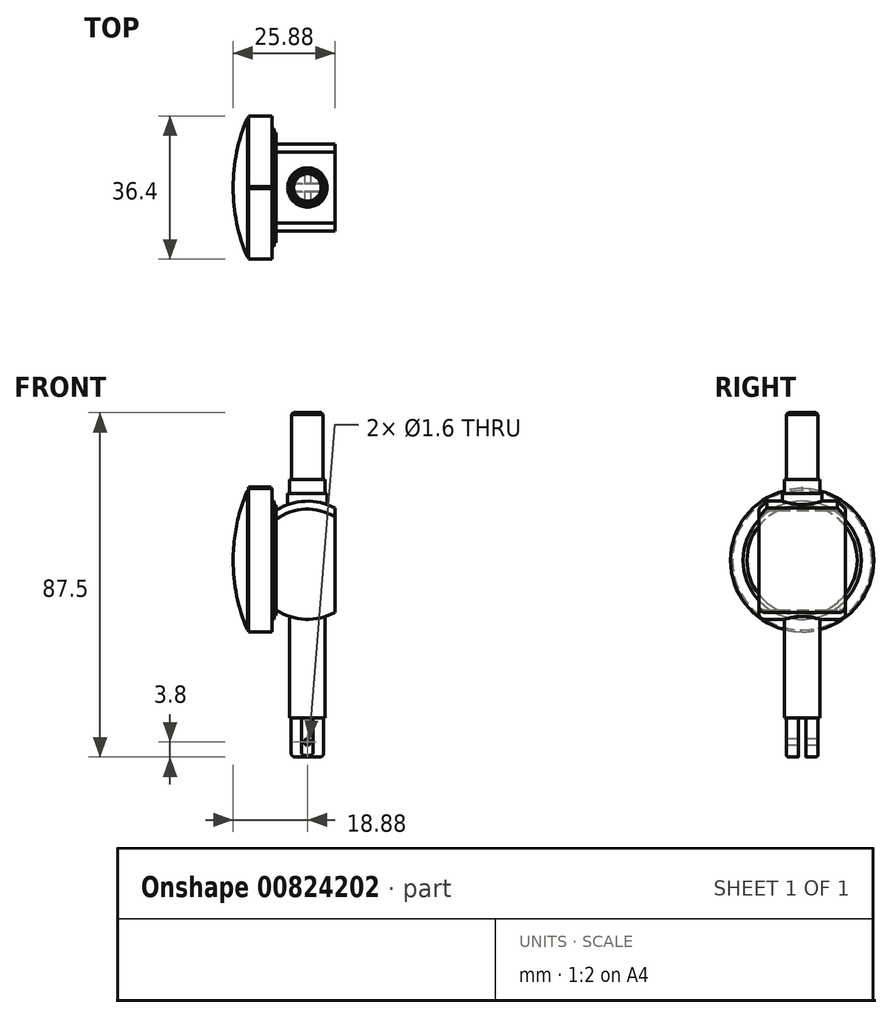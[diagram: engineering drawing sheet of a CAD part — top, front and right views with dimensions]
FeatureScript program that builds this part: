
annotation { "Feature Type Name" : "Feature", "Feature Type Description" : "" }
export const myFeature = defineFeature(function(context is Context, id is Id, definition is map)
    precondition{}
    {
        {
            var Q0;
            Q0=qCreatedBy(makeId("Front.planeOp"),FACE);
            var sketch = newSketch(context, id + "F0", { "sketchPlane" : qUnion([Q0])});
            skArc(sketch, "E0", {"start": v(7, 13.27) * mm, "mid": v(-0.58, 14.99) * mm, "end": v(-8, 12.69) * mm});
            skLineSegment(sketch, "E1", {"start": v(7, 13.27) * mm, "end": v(7, -13.27) * mm});
            skLineSegment(sketch, "E2", {"start": v(-8, 12.69) * mm, "end": v(-8, -12.69) * mm});
            skArc(sketch, "E3.trimOffspring", {"start": v(-8, -12.69) * mm, "mid": v(-0.58, -14.99) * mm, "end": v(7, -13.27) * mm});
            skSolve(sketch);
        }
        {
            var Q0;
            Q0=makeQuery(id+"F0.imprint","IMPRINT",FACE,{"disambiguationData":[TD([[makeQuery(id+"F0.imprint","IMPRINT",EDGE,{"derivedFrom":sQuery(id+"F0.wireOp",EDGE,"E0")}),1.0]])]});
            extrude(context, id + "F1", {"entities" : qUnion([Q0]), "endBound" : BoundingType.SYMMETRIC, "depth" : 22 * mm, "offsetDistance" : 25 * mm});
        }
        {
            var Q0;
            Q0=makeQuery(id+"F1.opExtrude","CAP_EDGE",EDGE,{"disambiguationData":[OSD([sQuery(id+"F0.wireOp",EDGE,"E0")])],"isStart":false});
            var Q1;
            Q1=makeQuery(id+"F1.opExtrude","CAP_EDGE",EDGE,{"disambiguationData":[OSD([sQuery(id+"F0.wireOp",EDGE,"E0")])],"isStart":true});
            chamfer(context, id + "F2", {"entities" : qUnion([Q0, Q1]), "width" : 2 * mm, "tangentPropagation" : true});
        }
        {
            var Q0;
            Q0=makeQuery(id+"F1.opExtrude","CAP_EDGE",EDGE,{"disambiguationData":[OSD([sQuery(id+"F0.wireOp",EDGE,"E3.trimOffspring")])],"isStart":false});
            var Q1;
            Q1=makeQuery(id+"F1.opExtrude","CAP_EDGE",EDGE,{"disambiguationData":[OSD([sQuery(id+"F0.wireOp",EDGE,"E3.trimOffspring")])],"isStart":true});
            fillet(context, id + "F3", {"entities" : qUnion([Q0, Q1]), "radius" : 1.5 * mm, "tangentPropagation" : true, "allowEdgeOverflow" : false});
        }
        {
            var Q0;
            Q0=qCreatedBy(makeId("Top.planeOp"),FACE);
            var sketch = newSketch(context, id + "F4", { "sketchPlane" : qUnion([Q0])});
            skCircle(sketch, "E4", {"center": v(0, 0) * mm, "radius": 5 * mm});
            skSolve(sketch);
        }
        {
            var Q0;
            Q0 = qSketchRegion(id + "F4", true);
            extrude(context, id + "F5", {"entities" : qUnion([Q0]), "operationType" : NewBodyOperationType.ADD, "depth" : 17 * mm, "offsetDistance" : 25 * mm});
        }
        {
            var Q0;
            Q0=makeQuery(id+"F5.opExtrude","CAP_FACE",FACE,{"disambiguationData":[OSD([sQuery(id+"F4.wireOp",EDGE,"E4")])],"isStart":false});
            var sketch = newSketch(context, id + "F6", { "sketchPlane" : qUnion([Q0])});
            skCircle(sketch, "E5", {"center": v(0, 0) * mm, "radius": 4.5 * mm});
            skSolve(sketch);
        }
        {
            var Q0;
            Q0=makeQuery(id+"F6.imprint","IMPRINT",FACE,{"disambiguationData":[TD([[makeQuery(id+"F6.imprint","IMPRINT",EDGE,{"derivedFrom":sQuery(id+"F6.wireOp",EDGE,"E5")}),1.0]])]});
            extrude(context, id + "F7", {"entities" : qUnion([Q0]), "operationType" : NewBodyOperationType.ADD, "depth" : 3.5 * mm, "offsetDistance" : 25 * mm});
        }
        {
            var Q0;
            Q0=makeQuery(id+"F7.opExtrude","CAP_FACE",FACE,{"disambiguationData":[OSD([sQuery(id+"F6.wireOp",EDGE,"E5")])],"isStart":false});
            var sketch = newSketch(context, id + "F8", { "sketchPlane" : qUnion([Q0])});
            skCircle(sketch, "E6", {"center": v(0, 0) * mm, "radius": 4 * mm});
            skSolve(sketch);
        }
        {
            var Q0;
            Q0=makeQuery(id+"F8.imprint","IMPRINT",FACE,{"disambiguationData":[TD([[makeQuery(id+"F8.imprint","IMPRINT",EDGE,{"derivedFrom":sQuery(id+"F8.wireOp",EDGE,"E6")}),1.0]])]});
            var Q1;
            Q1 = qSketchRegion(id + "F11", true);
            extrude(context, id + "F9", {"entities" : qUnion([Q0, Q1]), "operationType" : NewBodyOperationType.ADD, "depth" : 17 * mm, "offsetDistance" : 25 * mm});
        }
        {
            var Q0;
            Q0=makeQuery(id+"F9.opExtrude","CAP_EDGE",EDGE,{"disambiguationData":[OSD([sQuery(id+"F8.wireOp",EDGE,"E6")])],"isStart":false});
            chamfer(context, id + "F10", {"entities" : qUnion([Q0]), "width" : 0.5 * mm, "tangentPropagation" : true});
        }
        {
            var Q0;
            Q0=qCreatedBy(makeId("Top.planeOp"),FACE);
            var sketch = newSketch(context, id + "F11", { "sketchPlane" : qUnion([Q0])});
            skCircle(sketch, "E7", {"center": v(0, 0) * mm, "radius": 4.5 * mm});
            skSolve(sketch);
        }
        {
            var Q0;
            Q0 = qSketchRegion(id + "F11", true);
            extrude(context, id + "F12", {"entities" : qUnion([Q0]), "operationType" : NewBodyOperationType.ADD, "oppositeDirection" : true, "depth" : 40 * mm, "offsetDistance" : 25 * mm});
        }
        {
            var Q0;
            Q0=makeQuery(id+"F12.opExtrude","CAP_FACE",FACE,{"disambiguationData":[OSD([sQuery(id+"F11.wireOp",EDGE,"E7")])],"isStart":false});
            var sketch = newSketch(context, id + "F13", { "sketchPlane" : qUnion([Q0])});
            skCircle(sketch, "E8", {"center": v(0, 0) * mm, "radius": 4.25 * mm});
            skSolve(sketch);
        }
        {
            var Q0;
            Q0=makeQuery(id+"F13.imprint","IMPRINT",FACE,{"disambiguationData":[TD([[makeQuery(id+"F13.imprint","IMPRINT",EDGE,{"derivedFrom":sQuery(id+"F13.wireOp",EDGE,"E8")}),1.0]])]});
            extrude(context, id + "F14", {"entities" : qUnion([Q0]), "operationType" : NewBodyOperationType.ADD, "depth" : 10 * mm, "offsetDistance" : 25 * mm});
        }
        {
            var Q0;
            Q0=makeQuery(id+"F14.opExtrude","CAP_EDGE",EDGE,{"disambiguationData":[OSD([sQuery(id+"F13.wireOp",EDGE,"E8")])],"isStart":false});
            fillet(context, id + "F15", {"entities" : qUnion([Q0]), "radius" : 1 * mm, "tangentPropagation" : true, "allowEdgeOverflow" : false});
        }
        {
            var Q0;
            Q0=qCreatedBy(makeId("Front.planeOp"),FACE);
            var sketch = newSketch(context, id + "F16", { "sketchPlane" : qUnion([Q0])});
            skLineSegment(sketch, "E9.0", {"start": v(-8, 10.25) * mm, "end": v(-8, -10.87) * mm});
            skLineSegment(sketch, "E10", {"start": v(-8, 0) * mm, "end": v(-8, 14) * mm});
            skLineSegment(sketch, "E11", {"start": v(-8, 14) * mm, "end": v(-8.5, 14) * mm});
            skLineSegment(sketch, "E12", {"start": v(-8.5, 14) * mm, "end": v(-8.5, 15) * mm});
            skLineSegment(sketch, "E13", {"start": v(-8.5, 15) * mm, "end": v(-9, 15) * mm});
            skLineSegment(sketch, "E14", {"start": v(-9, 15) * mm, "end": v(-9, 18.2) * mm});
            skLineSegment(sketch, "E15", {"start": v(-15, 18.2) * mm, "end": v(-9, 18.2) * mm});
            skLineSegment(sketch, "E16", {"start": v(-15, 17.7) * mm, "end": v(-15.25, 17.7) * mm});
            skLineSegment(sketch, "E17", {"start": v(-15, 18.2) * mm, "end": v(-15, 17.7) * mm});
            skLineSegment(sketch, "E18", {"start": v(-8, 0) * mm, "end": v(-18.88, 0) * mm});
            skArc(sketch, "E19", {"start": v(-15.25, 17.7) * mm, "mid": v(-17.96, 9.03) * mm, "end": v(-18.88, 0) * mm});
            skSolve(sketch);
        }
        {
            var Q0;
            {var subQ0=sQuery(id+"F16.wireOp",EDGE,"E11");Q0=makeQuery(id+"F16.imprint","IMPRINT",FACE,{"disambiguationData":[TD([[makeQuery(id+"F16.imprint","IMPRINT",EDGE,{"derivedFrom":subQ0}),1.0]])]});}
            var Q1;
            Q1=sQuery(id+"F16.wireOp",EDGE,"E18");
            revolve(context, id + "F17", {"operationType" : NewBodyOperationType.ADD, "surfaceOperationType" : NewSurfaceOperationType.NEW, "entities" : qUnion([Q0]), "axis" : qUnion([Q1]), "revolveType" : RevolveType.FULL});
        }
        {
            var Q0;
            Q0=qCreatedBy(makeId("Right.planeOp"),FACE);
            var sketch = newSketch(context, id + "F18", { "sketchPlane" : qUnion([Q0])});
            skLineSegment(sketch, "E20.0", {"start": v(-4.5, -40) * mm, "end": v(4.5, -40) * mm, "construction": true});
            skLineSegment(sketch, "E21.bottom", {"start": v(-1, -40) * mm, "end": v(1, -40) * mm});
            skLineSegment(sketch, "E21.top", {"start": v(-1, -51) * mm, "end": v(1, -51) * mm});
            skLineSegment(sketch, "E21.left", {"start": v(-1, -40) * mm, "end": v(-1, -51) * mm});
            skLineSegment(sketch, "E21.right", {"start": v(1, -40) * mm, "end": v(1, -51) * mm});
            skLineSegment(sketch, "E22.bottom", {"start": v(-4, -40) * mm, "end": v(-6, -40) * mm});
            skLineSegment(sketch, "E22.top", {"start": v(-4, -51) * mm, "end": v(-6, -51) * mm});
            skLineSegment(sketch, "E22.left", {"start": v(-4, -40) * mm, "end": v(-4, -51) * mm});
            skLineSegment(sketch, "E22.right", {"start": v(-6, -40) * mm, "end": v(-6, -51) * mm});
            skLineSegment(sketch, "E23.bottom", {"start": v(4, -40) * mm, "end": v(6, -40) * mm});
            skLineSegment(sketch, "E23.top", {"start": v(4, -51) * mm, "end": v(6, -51) * mm});
            skLineSegment(sketch, "E23.left", {"start": v(4, -40) * mm, "end": v(4, -51) * mm});
            skLineSegment(sketch, "E23.right", {"start": v(6, -40) * mm, "end": v(6, -51) * mm});
            skLineSegment(sketch, "E24.0", {"start": v(3.25, -50) * mm, "end": v(-3.25, -50) * mm, "construction": true});
            skLineSegment(sketch, "E25", {"start": v(-4.5, -40) * mm, "end": v(-1, -40) * mm});
            skLineSegment(sketch, "E26", {"start": v(1, -40) * mm, "end": v(4.5, -40) * mm});
            skLineSegment(sketch, "E27", {"start": v(-4, -42.75) * mm, "end": v(-1, -42.75) * mm, "construction": true});
            skLineSegment(sketch, "E28", {"start": v(1, -45.5) * mm, "end": v(4, -45.5) * mm, "construction": true});
            skSolve(sketch);
        }
        {
            var Q0;
            Q0 = qSketchRegion(id + "F18", true);
            extrude(context, id + "F19", {"entities" : qUnion([Q0]), "operationType" : NewBodyOperationType.REMOVE, "endBound" : BoundingType.SYMMETRIC, "oppositeDirection" : true, "depth" : 25 * mm, "offsetDistance" : 25 * mm});
        }
        {
            var Q0;
            Q0=makeQuery(id+"F19.boolean.opBoolean","COPY",FACE,{"derivedFrom":makeQuery(id+"F19.opExtrude","SWEPT_FACE",FACE,{"disambiguationData":[OSD([sQuery(id+"F18.wireOp",EDGE,"E22.left")])]})});
            var sketch = newSketch(context, id + "F20", { "sketchPlane" : qUnion([Q0])});
            skCircle(sketch, "E29", {"center": v(0, -46.2) * mm, "radius": 0.8 * mm});
            skLineSegment(sketch, "E30.0", {"start": v(3.1, -50) * mm, "end": v(-3.1, -50) * mm});
            skSolve(sketch);
        }
        {
            var Q0;
            Q0=makeQuery(id+"F20.imprint","IMPRINT",FACE,{"disambiguationData":[TD([[makeQuery(id+"F20.imprint","IMPRINT",EDGE,{"derivedFrom":sQuery(id+"F20.wireOp",EDGE,"E29")}),1.0]])]});
            extrude(context, id + "F21", {"entities" : qUnion([Q0]), "operationType" : NewBodyOperationType.REMOVE, "endBound" : BoundingType.THROUGH_ALL, "oppositeDirection" : true, "depth" : 25 * mm, "offsetDistance" : 25 * mm});
        }
        {
            var Q0;
            Q0=makeQuery(id+"F17.opRevolve","SWEPT_FACE",FACE,{"disambiguationData":[OSD([sQuery(id+"F16.wireOp",EDGE,"E17")])]});
            var sketch = newSketch(context, id + "F22", { "sketchPlane" : qUnion([Q0])});
            skCircle(sketch, "E31.0", {"center": v(0, 0) * mm, "radius": 18.2 * mm});
            skLineSegment(sketch, "E32", {"start": v(-0.29, 18.2) * mm, "end": v(0, 18.6) * mm});
            skLineSegment(sketch, "E33", {"start": v(0, 18.6) * mm, "end": v(0.29, 18.2) * mm});
            skSolve(sketch);
        }
        {
            var Q0;
            {var subQ0=sQuery(id+"F22.wireOp",EDGE,"E32");Q0=makeQuery(id+"F22.imprint","IMPRINT",FACE,{"disambiguationData":[TD([[makeQuery(id+"F22.imprint","IMPRINT",EDGE,{"derivedFrom":subQ0}),-1.0]])]});}
            extrude(context, id + "F23", {"entities" : qUnion([Q0]), "operationType" : NewBodyOperationType.ADD, "oppositeDirection" : true, "depth" : 5.8 * mm, "offsetDistance" : 25 * mm});
        }
    });
